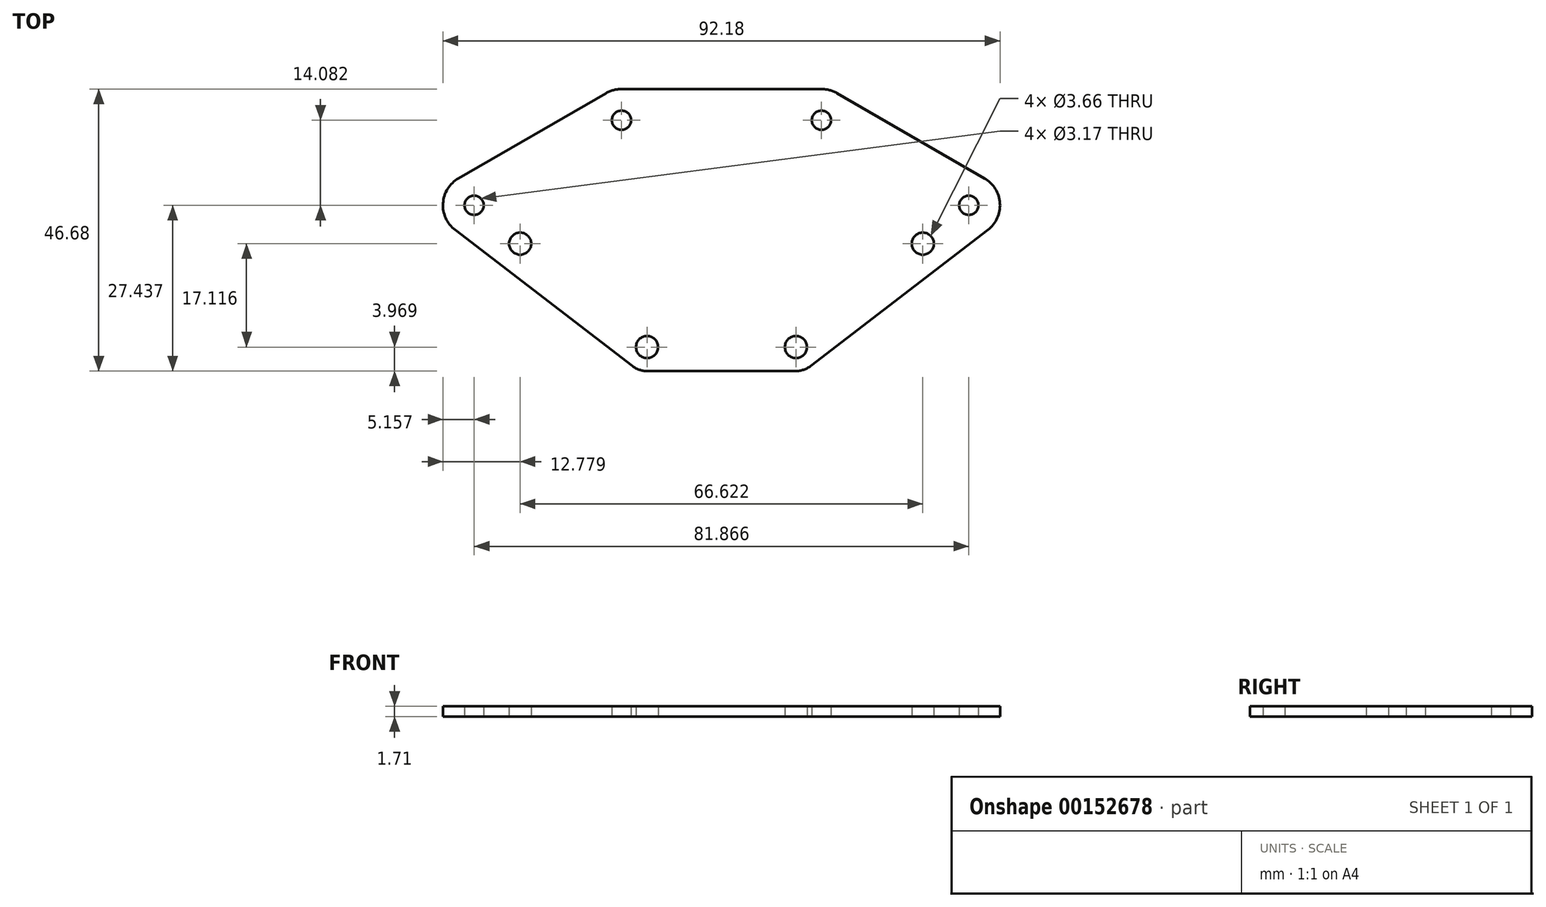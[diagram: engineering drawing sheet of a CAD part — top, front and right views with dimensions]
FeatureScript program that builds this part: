
annotation { "Feature Type Name" : "Feature", "Feature Type Description" : "" }
export const myFeature = defineFeature(function(context is Context, id is Id, definition is map)
    precondition{}
    {
        {
            var Q0;
            Q0=qCreatedBy(makeId("Top.planeOp"),FACE);
            var sketch = newSketch(context, id + "F0", { "sketchPlane" : qUnion([Q0])});
            skLineSegment(sketch, "E0.bottom", {"start": v(20.32, -1.02) * mm, "end": v(23.75, -1.02) * mm, "construction": true});
            skLineSegment(sketch, "E0.top", {"start": v(20.32, 1.02) * mm, "end": v(23.75, 1.02) * mm, "construction": true});
            skLineSegment(sketch, "E0.left", {"start": v(20.32, -1.02) * mm, "end": v(20.32, 1.02) * mm, "construction": true});
            skLineSegment(sketch, "E0.right", {"start": v(23.75, -1.02) * mm, "end": v(23.75, 1.02) * mm, "construction": true});
            skLineSegment(sketch, "E1.top", {"start": v(20.32, -9.78) * mm, "end": v(-20.32, -9.78) * mm, "construction": true});
            skLineSegment(sketch, "E1.left", {"start": v(20.32, -1.02) * mm, "end": v(20.32, -9.78) * mm, "construction": true});
            skLineSegment(sketch, "E1.right", {"start": v(-20.32, -1.02) * mm, "end": v(-20.32, -9.78) * mm, "construction": true});
            skLineSegment(sketch, "E2.bottom", {"start": v(-20.32, -1.02) * mm, "end": v(-23.75, -1.02) * mm, "construction": true});
            skLineSegment(sketch, "E2.top", {"start": v(-20.32, 1.02) * mm, "end": v(-23.75, 1.02) * mm, "construction": true});
            skLineSegment(sketch, "E2.left", {"start": v(-20.32, -1.02) * mm, "end": v(-20.32, 1.02) * mm, "construction": true});
            skLineSegment(sketch, "E2.right", {"start": v(-23.75, -1.02) * mm, "end": v(-23.75, 1.02) * mm, "construction": true});
            skLineSegment(sketch, "E3.top", {"start": v(20.32, 9.78) * mm, "end": v(-20.32, 9.78) * mm, "construction": true});
            skLineSegment(sketch, "E3.left", {"start": v(20.32, 1.02) * mm, "end": v(20.32, 9.78) * mm, "construction": true});
            skLineSegment(sketch, "E3.right", {"start": v(-20.32, 1.02) * mm, "end": v(-20.32, 9.78) * mm, "construction": true});
            skArc(sketch, "E4", {"start": v(23.75, -1.02) * mm, "mid": v(24.77, 0) * mm, "end": v(23.75, 1.02) * mm, "construction": true});
            skArc(sketch, "E5", {"start": v(-23.75, 1.02) * mm, "mid": v(-24.76, 0) * mm, "end": v(-23.75, -1.02) * mm, "construction": true});
            skLineSegment(sketch, "E6", {"start": v(0, -9.78) * mm, "end": v(0, 9.78) * mm, "construction": true});
            skLineSegment(sketch, "E7.bottom", {"start": v(24.9, 4.89) * mm, "end": v(-24.9, 4.89) * mm, "construction": true});
            skLineSegment(sketch, "E7.top", {"start": v(24.9, -4.89) * mm, "end": v(-24.9, -4.89) * mm, "construction": true});
            skLineSegment(sketch, "E7.left", {"start": v(24.9, 4.89) * mm, "end": v(24.9, -4.89) * mm, "construction": true});
            skLineSegment(sketch, "E7.right", {"start": v(-24.9, 4.89) * mm, "end": v(-24.9, -4.89) * mm, "construction": true});
            skPoint(sketch, "E7.middle", {"position": v(0, 0) * mm});
            skCircle(sketch, "E8", {"center": v(-24.9, 4.89) * mm, "radius": 1.73 * mm, "construction": true});
            skCircle(sketch, "E9", {"center": v(-24.9, -4.89) * mm, "radius": 1.73 * mm, "construction": true});
            skCircle(sketch, "E10", {"center": v(24.9, -4.89) * mm, "radius": 1.73 * mm, "construction": true});
            skCircle(sketch, "E11", {"center": v(24.9, 4.89) * mm, "radius": 1.73 * mm, "construction": true});
            skLineSegment(sketch, "E12", {"start": v(-20.32, 0) * mm, "end": v(-10.9, 0) * mm, "construction": true});
            skLineSegment(sketch, "E13", {"start": v(0, 9.78) * mm, "end": v(0, 23) * mm, "construction": true});
            skLineSegment(sketch, "E14", {"start": v(-16.54, 23) * mm, "end": v(16.54, 23) * mm, "construction": true});
            skLineSegment(sketch, "E15", {"start": v(16.54, 23) * mm, "end": v(40.93, 8.93) * mm, "construction": true});
            skLineSegment(sketch, "E16", {"start": v(-16.54, 23) * mm, "end": v(-40.93, 8.93) * mm, "construction": true});
            skCircle(sketch, "E17", {"center": v(40.93, 8.93) * mm, "radius": 1.59 * mm});
            skCircle(sketch, "E18", {"center": v(16.54, 23) * mm, "radius": 1.59 * mm});
            skCircle(sketch, "E19", {"center": v(-16.54, 23) * mm, "radius": 1.59 * mm});
            skCircle(sketch, "E20", {"center": v(-40.93, 8.93) * mm, "radius": 1.59 * mm});
            skLineSegment(sketch, "E21", {"start": v(-16.54, 23) * mm, "end": v(-10.9, 0) * mm, "construction": true});
            skLineSegment(sketch, "E22", {"start": v(0, 23) * mm, "end": v(0, 28.17) * mm, "construction": true});
            skLineSegment(sketch, "E23", {"start": v(40.93, 8.93) * mm, "end": v(0, 8.93) * mm, "construction": true});
            skLineSegment(sketch, "E24", {"start": v(0, 8.93) * mm, "end": v(-40.93, 8.93) * mm, "construction": true});
            skLineSegment(sketch, "E25", {"start": v(-16.54, 28.17) * mm, "end": v(16.54, 28.17) * mm});
            skArc(sketch, "E26", {"start": v(44.07, 4.83) * mm, "mid": v(46.08, 9.26) * mm, "end": v(43.51, 13.4) * mm});
            skArc(sketch, "E27", {"start": v(19.12, 27.48) * mm, "mid": v(17.88, 28) * mm, "end": v(16.54, 28.17) * mm});
            skArc(sketch, "E28", {"start": v(-16.54, 28.17) * mm, "mid": v(-17.88, 28) * mm, "end": v(-19.12, 27.48) * mm});
            skArc(sketch, "E29", {"start": v(-43.51, 13.4) * mm, "mid": v(-46.08, 9.26) * mm, "end": v(-44.07, 4.83) * mm});
            skLineSegment(sketch, "E30", {"start": v(19.12, 27.48) * mm, "end": v(43.51, 13.4) * mm});
            skLineSegment(sketch, "E31", {"start": v(-19.12, 27.48) * mm, "end": v(-43.51, 13.4) * mm});
            skLineSegment(sketch, "E32", {"start": v(-44.07, 4.83) * mm, "end": v(-14.74, -17.69) * mm});
            skLineSegment(sketch, "E33", {"start": v(44.07, 4.83) * mm, "end": v(14.74, -17.69) * mm});
            skArc(sketch, "E34", {"start": v(-14.74, -17.69) * mm, "mid": v(-13.6, -18.3) * mm, "end": v(-12.32, -18.51) * mm});
            skArc(sketch, "E35", {"start": v(12.32, -18.51) * mm, "mid": v(13.6, -18.3) * mm, "end": v(14.74, -17.69) * mm});
            skLineSegment(sketch, "E36", {"start": v(0, -9.78) * mm, "end": v(0, -14.54) * mm, "construction": true});
            skLineSegment(sketch, "E37", {"start": v(-12.32, -14.54) * mm, "end": v(12.32, -14.54) * mm, "construction": true});
            skLineSegment(sketch, "E38", {"start": v(0, -14.54) * mm, "end": v(0, -18.51) * mm, "construction": true});
            skLineSegment(sketch, "E39", {"start": v(-12.32, -18.51) * mm, "end": v(12.32, -18.51) * mm});
            skCircle(sketch, "E40", {"center": v(-12.32, -14.54) * mm, "radius": 1.83 * mm});
            skCircle(sketch, "E41", {"center": v(12.32, -14.54) * mm, "radius": 1.83 * mm});
            skCircle(sketch, "E42", {"center": v(24.9, -4.89) * mm, "radius": 3.97 * mm, "construction": true});
            skLineSegment(sketch, "E43", {"start": v(24.9, -4.89) * mm, "end": v(33.31, 2.57) * mm, "construction": true});
            skCircle(sketch, "E44", {"center": v(33.31, 2.57) * mm, "radius": 4.76 * mm, "construction": true});
            skCircle(sketch, "E45", {"center": v(33.31, 2.57) * mm, "radius": 1.83 * mm});
            skLineSegment(sketch, "E46", {"start": v(-24.9, -4.89) * mm, "end": v(-33.31, 2.57) * mm, "construction": true});
            skCircle(sketch, "E47", {"center": v(-33.31, 2.57) * mm, "radius": 4.76 * mm, "construction": true});
            skCircle(sketch, "E48", {"center": v(-33.31, 2.57) * mm, "radius": 1.83 * mm});
            skCircle(sketch, "E49", {"center": v(24.9, 4.89) * mm, "radius": 3.97 * mm, "construction": true});
            skArc(sketch, "E50", {"start": v(43.51, 13.4) * mm, "mid": v(35.78, 8.59) * mm, "end": v(44.07, 4.83) * mm, "construction": true});
            skSolve(sketch);
        }
        {
            var Q0;
            Q0=qSketchRegion(id+"F0",true);
            extrude(context, id + "F1", {"entities" : qUnion([Q0]), "depth" : 1.7 * mm});
        }
    });
